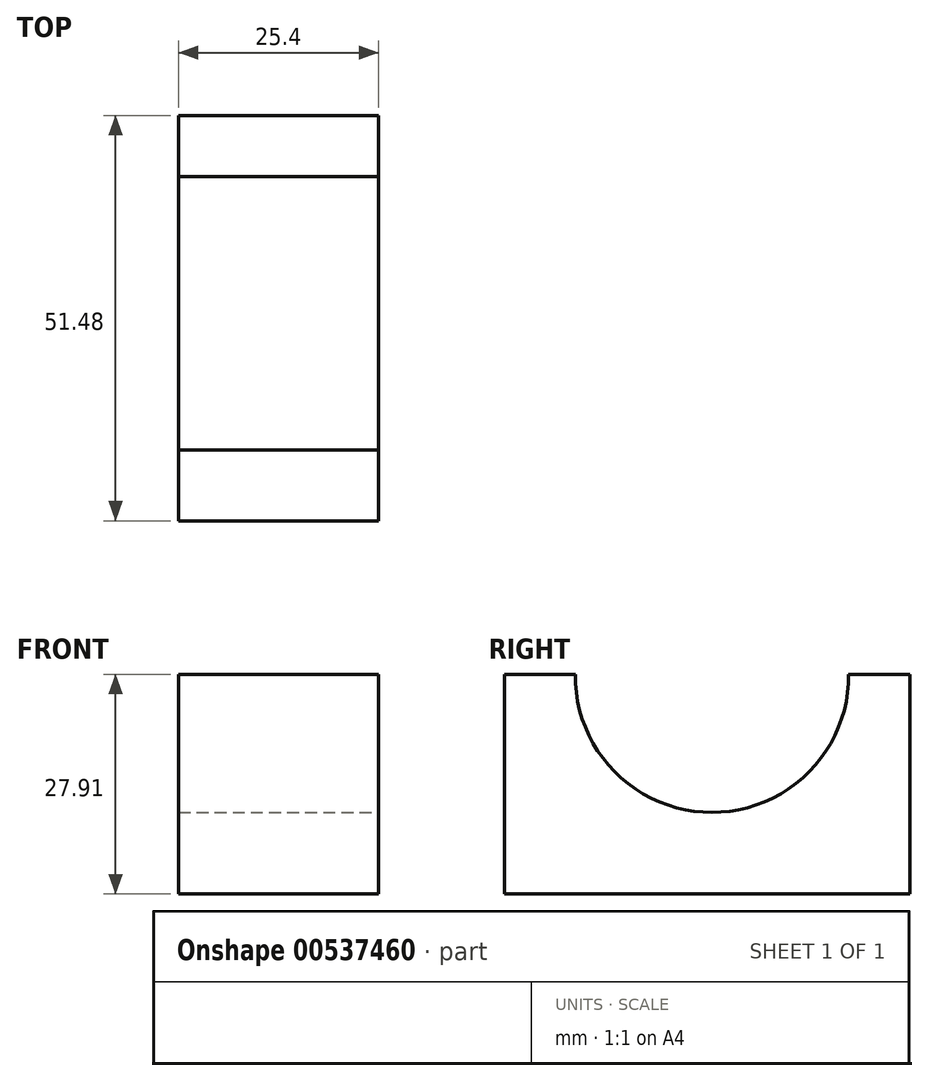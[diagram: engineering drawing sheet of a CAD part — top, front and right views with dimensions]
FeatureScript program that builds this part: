
annotation { "Feature Type Name" : "Feature", "Feature Type Description" : "" }
export const myFeature = defineFeature(function(context is Context, id is Id, definition is map)
    precondition{}
    {
        {
            var Q0;
            Q0=qCreatedBy(makeId("Right.planeOp"),FACE);
            var sketch = newSketch(context, id + "F0", { "sketchPlane" : qUnion([Q0])});
            skLineSegment(sketch, "E0", {"start": v(0, 0) * mm, "end": v(51.48, 0) * mm});
            skLineSegment(sketch, "E1", {"start": v(51.48, 0) * mm, "end": v(51.48, 27.91) * mm});
            skLineSegment(sketch, "E2", {"start": v(51.48, 27.91) * mm, "end": v(0, 27.91) * mm});
            skLineSegment(sketch, "E3", {"start": v(0, 27.91) * mm, "end": v(0, 0) * mm});
            skSolve(sketch);
        }
        {
            var Q0;
            Q0 = qSketchRegion(id + "F0", true);
            extrude(context, id + "F1", {"entities" : qUnion([Q0]), "depth" : 25.4 * mm, "offsetDistance" : 25.4 * mm});
        }
        {
            var Q0;
            Q0=makeQuery(id+"F1.opExtrude","CAP_FACE",FACE,{"disambiguationData":[OSD([sQuery(id+"F0.wireOp",EDGE,"E0"),sQuery(id+"F0.wireOp",EDGE,"E1"),sQuery(id+"F0.wireOp",EDGE,"E2"),sQuery(id+"F0.wireOp",EDGE,"E3")])],"isStart":false});
            var sketch = newSketch(context, id + "F2", { "sketchPlane" : qUnion([Q0])});
            skCircle(sketch, "E4", {"center": v(26.36, 27.73) * mm, "radius": 17.37 * mm});
            skPoint(sketch, "E4.first.point", {"position": v(9, 27.91) * mm});
            skPoint(sketch, "E4.second.point", {"position": v(43.73, 27.91) * mm});
            skPoint(sketch, "E4.third.point", {"position": v(23.88, 10.54) * mm});
            skSolve(sketch);
        }
        {
            var Q0;
            {var subQ0=sQuery(id+"F2.wireOp",EDGE,"E4");var subQ1=makeQuery(id+"F1.opExtrude","CAP_EDGE",EDGE,{"disambiguationData":[OSD([sQuery(id+"F0.wireOp",EDGE,"E2")])],"isStart":false});var subQ2=makeQuery(id+"F2.imprint","INTERSECT",VERTEX,{"disambiguationData":[OD(0.0)],"derivedFrom":[subQ1,subQ0]});Q0=makeQuery(id+"F2.imprint","IMPRINT",FACE,{"disambiguationData":[TD([[makeQuery(id+"F2.imprint","IMPRINT",EDGE,{"disambiguationData":[TD([[subQ2,-1.0]])],"derivedFrom":subQ0}),1.0]])]});}
            var Q1;
            {var subQ0=sQuery(id+"F2.wireOp",EDGE,"E4");var subQ1=makeQuery(id+"F1.opExtrude","CAP_EDGE",EDGE,{"disambiguationData":[OSD([sQuery(id+"F0.wireOp",EDGE,"E2")])],"isStart":false});var subQ2=makeQuery(id+"F2.imprint","INTERSECT",VERTEX,{"disambiguationData":[OD(0.0)],"derivedFrom":[subQ1,subQ0]});Q1=makeQuery(id+"F2.imprint","IMPRINT",FACE,{"disambiguationData":[TD([[makeQuery(id+"F2.imprint","IMPRINT",EDGE,{"disambiguationData":[TD([[subQ2,1.0]])],"derivedFrom":subQ0}),1.0]])]});}
            extrude(context, id + "F3", {"entities" : qUnion([Q0, Q1]), "operationType" : NewBodyOperationType.REMOVE, "oppositeDirection" : true, "depth" : 25.4 * mm, "offsetDistance" : 25.4 * mm});
        }
    });
